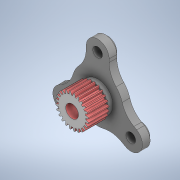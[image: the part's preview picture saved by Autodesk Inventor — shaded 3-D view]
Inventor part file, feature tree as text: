
AUTODESK INVENTOR PART (.ipt)
format: ipt  version: 2022 (Build 260153000, 153)  size: 419,328 bytes
history: mixed  units: mm
features: other x3, extrude x1, sketch x1, imported_body x1
ambient origin geometry x8: Origin, YZ Plane, XZ Plane, XY Plane, X Axis, Y Axis, Z Axis, Center Point
bodies: Solid1 (imported_parasolid)
feature tree (6):
  other  "Planet_Carrier_Modifed_with_sun_gear.iam"
  other  "Plamet_Carrier.ipt:1"
  other  "24_Teeth_Sun_Gear.ipt:1"
  extrude  "Extrusion1"  Depth=10.0mm TaperAngle=0.0deg
  sketch  "Sketch1"  dims[d0=10.0mm d1=7.0mm d2=0.0mm]
  imported_body  NMx_Import_Brep_tag  [imported B-rep: ~177 faces, bbox_mm=[31.788121, 26.496463, 14.0]]
